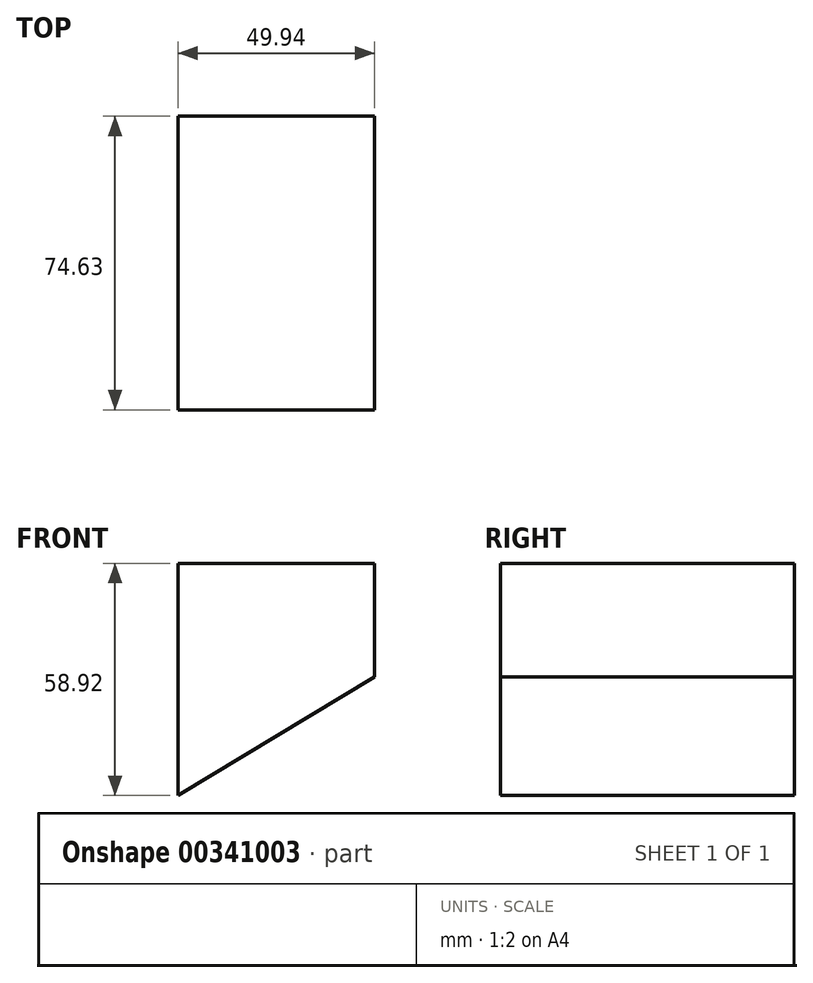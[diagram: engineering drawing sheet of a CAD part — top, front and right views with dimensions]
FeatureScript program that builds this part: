
annotation { "Feature Type Name" : "Feature", "Feature Type Description" : "" }
export const myFeature = defineFeature(function(context is Context, id is Id, definition is map)
    precondition{}
    {
        {
            var Q0;
            Q0=qCreatedBy(makeId("Front.planeOp"),FACE);
            var sketch = newSketch(context, id + "F0", { "sketchPlane" : qUnion([Q0])});
            skLineSegment(sketch, "E0", {"start": v(0, 0) * mm, "end": v(0, 58.92) * mm});
            skLineSegment(sketch, "E1", {"start": v(0, 58.92) * mm, "end": v(49.94, 58.92) * mm});
            skLineSegment(sketch, "E2", {"start": v(49.94, 58.92) * mm, "end": v(49.94, 30.12) * mm});
            skLineSegment(sketch, "E3", {"start": v(49.94, 30.12) * mm, "end": v(0, 0) * mm});
            skSolve(sketch);
        }
        {
            var Q0;
            Q0 = qSketchRegion(id + "F0", true);
            extrude(context, id + "F1", {"entities" : qUnion([Q0]), "depth" : 74.63 * mm});
        }
    });
